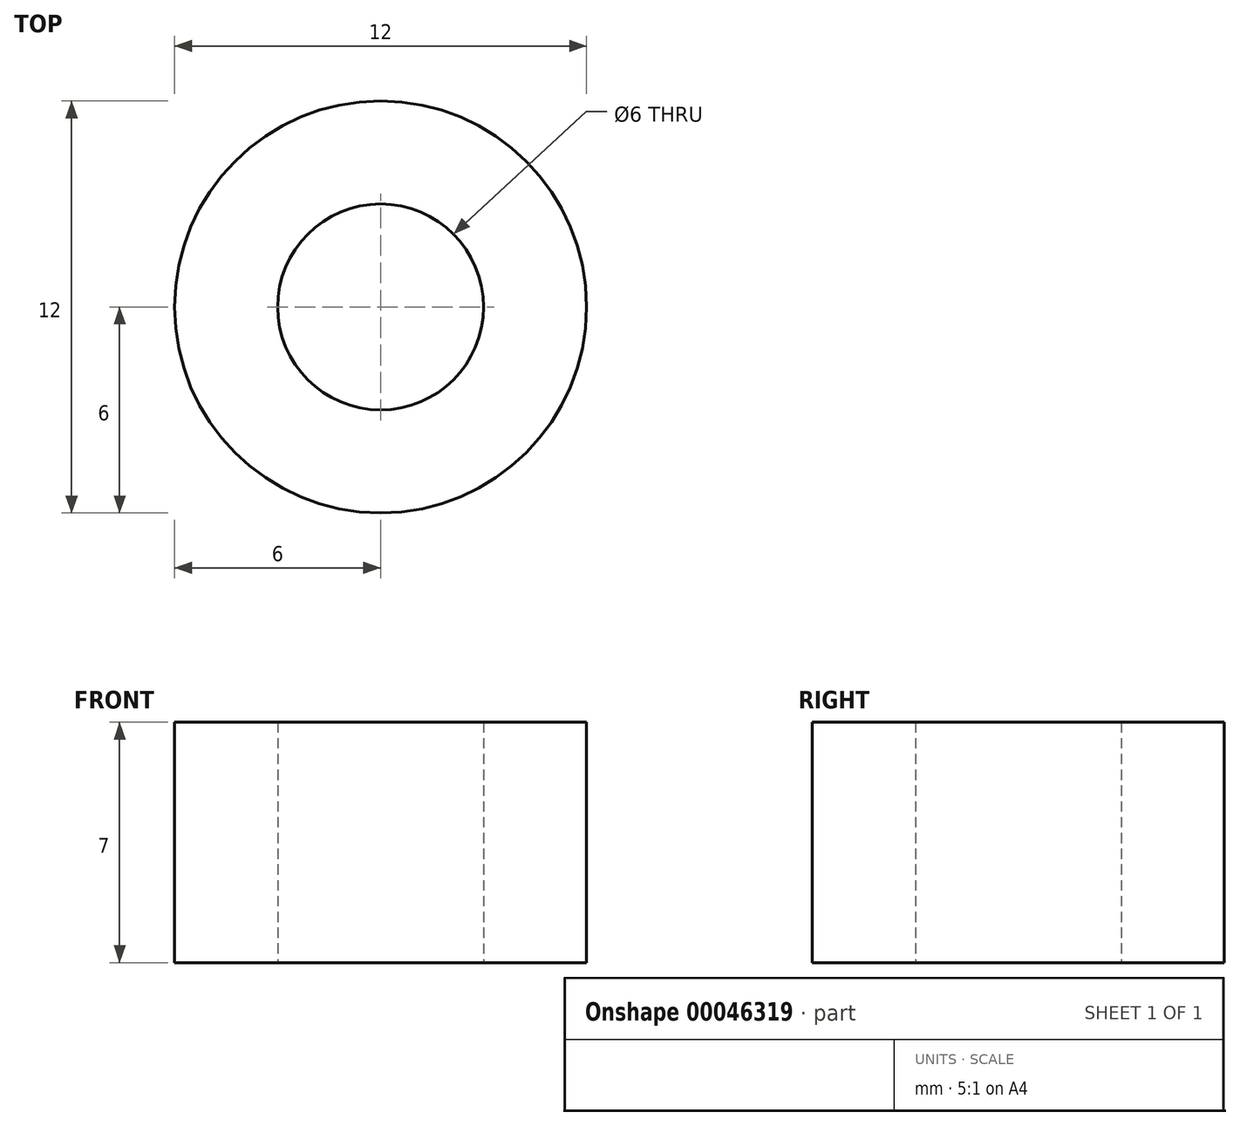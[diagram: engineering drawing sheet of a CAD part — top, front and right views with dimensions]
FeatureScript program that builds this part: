
annotation { "Feature Type Name" : "Feature", "Feature Type Description" : "" }
export const myFeature = defineFeature(function(context is Context, id is Id, definition is map)
    precondition{}
    {
        {
            var Q0;
            Q0=qCreatedBy(makeId("Top.planeOp"),FACE);
            var sketch = newSketch(context, id + "F0", { "sketchPlane" : qUnion([Q0])});
            skCircle(sketch, "E0", {"center": v(0, 0) * mm, "radius": 3 * mm});
            skCircle(sketch, "E1", {"center": v(0, 0) * mm, "radius": 6 * mm});
            skSolve(sketch);
        }
        {
            var Q0;
            Q0=makeQuery(id+"F0.imprint","IMPRINT",FACE,{"disambiguationData":[TD([[makeQuery(id+"F0.imprint","IMPRINT",EDGE,{"derivedFrom":sQuery(id+"F0.wireOp",EDGE,"E0")}),-1.0]])]});
            extrude(context, id + "F1", {"entities" : qUnion([Q0]), "flatOperationType" : FlatOperationType.REMOVE, "offsetDistance" : 25 * mm, "depth" : 7 * mm, "domain" : OperationDomain.MODEL});
        }
    });
